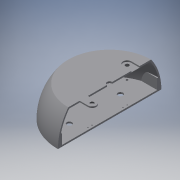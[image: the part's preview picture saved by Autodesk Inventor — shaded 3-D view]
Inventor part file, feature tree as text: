
AUTODESK INVENTOR PART (.ipt)
format: ipt  version: 2019 (Build 230136000, 136)  size: 576,512 bytes
history: native  units: mm
features: sketch x29, extrude x24, other x9, hole x4, projected_geometry x3, reference x2, revolve x1, loft x1, shell x1, mirror x1, fillet x1
ambient origin geometry x8: Origin, YZ Plane, XZ Plane, XY Plane, X Axis, Y Axis, Z Axis, Center Point
bodies: Body1 (feature_tree)
feature tree (76):
  revolve  "Вращение3"
  extrude  "Выдавливание106"  Depth=170.0mm
  extrude  "Выдавливание107"  Depth=100.0mm
  hole  "Отверстие2"  [1 undecoded]
  extrude  "Выдавливание108"  Depth=4.0mm
  hole  "Отверстие3"  [1 undecoded]
  hole  "Отверстие4"  [1 undecoded]
  hole  "Отверстие5"  [1 undecoded]
  extrude  "Выдавливание109"  TaperAngle=0.0deg  [1 undecoded]
  sketch  "Эскиз4"
  other  "РабПлоскость1"
  sketch  "Эскиз5"
  loft  "Лофт1"
  extrude  "Выдавливание2"  Depth=5.0mm
  shell  "Оболочка1"  Thickness=2.0mm
  sketch  "Эскиз21"
  extrude  "Выдавливание15"  Depth=2.0mm
  extrude  "Выдавливание16"  Depth=2.0mm
  other  "РабПлоскость7"
  sketch  "Эскиз23"
  extrude  "Выдавливание17"  Depth=20.0mm
  extrude  "Выдавливание18"  Depth=10.0mm TaperAngle=0.0deg
  sketch  "Эскиз24"
  extrude  "Выдавливание19"  Depth=10.0mm TaperAngle=0.0deg
  extrude  "Выдавливание20"  Depth=143.802871mm
  extrude  "Выдавливание21"  TaperAngle=0.0deg  [1 undecoded]
  mirror  "Зеркальное отражение2"
  other  "РабПлоскость12"
  sketch  "Эскиз42"
  extrude  "Выдавливание57"  Depth=1.0mm TaperAngle=0.0deg
  sketch  "Эскиз84"
  extrude  "Выдавливание75"  Depth=5.0mm
  extrude  "Выдавливание76"  Depth=5.0mm
  extrude  "Выдавливание77"  Depth=2.0mm
  extrude  "Выдавливание95"  Depth=2.0mm
  extrude  "Выдавливание96"  Depth=5.0mm
  extrude  "Выдавливание97"  Depth=1.0mm TaperAngle=0.0deg
  fillet  "Сопряжение3"  Radius=3.0mm
  extrude  "Выдавливание98"  Depth=2.0mm
  extrude  "Выдавливание101"  Depth=6.0mm
  other  "РабПлоскость25"
  extrude  "Выдавливание102"  Depth=1.0mm TaperAngle=0.0deg
  other  "РабПлоскость26"
  extrude  "Выдавливание103"  Depth=2.0mm
  extrude  "Выдавливание104"  Depth=2.0mm
  sketch  "Эскиз6"
  projected_geometry  "Спроецированная петля1"
  sketch  "Эскиз22"
  sketch  "Эскиз25"
  sketch  "Эскиз61"
  sketch  "Эскиз87"
  sketch  "Эскиз109"
  sketch  "Эскиз110"
  projected_geometry  "Спроецированная петля42"
  sketch  "Эскиз111"
  projected_geometry  "Спроецированная петля43"
  sketch  "Эскиз114"
  sketch  "Эскиз117"
  sketch  "Эскиз118"
  reference  "Ссылка1"
  reference  "Ссылка2"
  sketch  "Эскиз119"
  sketch  "Эскиз120"
  sketch  "Эскиз121"
  other  "Твердое тело3"
  sketch  "Эскиз124"
  sketch  "Эскиз125"
  sketch  "Эскиз126"
  sketch  "Эскиз127"
  sketch  "Эскиз128"
  sketch  "Эскиз129"
  sketch  "Эскиз130"
  sketch  "Эскиз131"
  other  "<userpath>\Desktop\САПР\Работы\ПД\робот\робот - сборка фулл.iam"
  other  "робот - сборка фулл.iam"
  other  "крепление-стенки:1"
note: 6 required parameter values undecoded (feature->parameter linkage not recoverable at this tier; creation-order binding heuristic only, values carry confidence <= 0.55)
